# Revit family: WAGNER_Извещатели_TITANUS PRO SENS_net
name_source: partatom
category: Оборудование
revit_build: Autodesk Revit 2017 (Build: 20170118_1100(x64)
units: mm (PartAtom-declared; Revit-internal decimal feet)

## family parameters
Всегда вертикально = Да
Заголовок OmniClass = Alarm Panels
На основе рабочей плоскости = Нет
Номер OmniClass = 23.85.30.21.11.14
Общий = Да
При загрузке вырезать с полостями = Нет
Размер круглого соединителя = Использовать диаметр
Тип детали = Нормальный
Точка расчета площади = Нет

## types (6) — shared parameters
ADSK_URL документации изделия = https://ru.wagnergroup.com
ADSK_URL страницы изделия = https://ru.wagnergroup.com
ADSK_Версия Revit = Revit 2017
ADSK_Версия семейства = Версия 1
ADSK_Дата изменения = 18.07.20
ADSK_Единица измерения = шт.
ADSK_Завод-изготовитель = WAGNER
ADSK_Код изделия = -
ADSK_Материал = WAGNER_Корпус
ADSK_Наименование = Извещатель пожарный дымовой аспирационный
ADSK_Наименование краткое = Извещатель пожарный
ADSK_Напряжение = 24 В
ADSK_Размер_Высота = 292 мм
ADSK_Размер_Длина = 200 мм
ADSK_Размер_Ширина = 113 мм
COBie Category = Fire alarm panels
Masterformat Code = 28 46 23
Masterformat Title = Fire Alarm Notification Appliances
OmniClass Code = 23.85.30.21.11.14
OmniClass Title = Alarm Panels
UNSPSC Code = 46191505
UNSPSC Title = Fire alarm systems
URL = www.wagner-russia.com
Uniclass Code = Pr_75_75_30_29
Uniclass Title = Fire alarm panels
WAGNER_Ip = Ip20 или Ip52
WAGNER_Классы проектирования  = А, B, C
WAGNER_Количество каналов обнаружения = 2
WAGNER_Количество сигналов (реле) неисправности = от 1 до 2
WAGNER_Питание = 24В
WAGNER_Расчет системы = Программа PipeCalc
WAGNER_Страна производства = Германия
bimon.ru = bimon.ru
Изготовитель = WAGNER
Описание = Извещатель пожарный дымовой аспирационный

## per-type parameters (varying)
| type | ADSK_Марка | WAGNER_Variation | WAGNER_Артикул | WAGNER_Количество сигналов (реле) тревоги | WAGNER_Модуль управления вентилятором | WAGNER_Название | WAGNER_Плата_сетевая_TITANUS_NU-5-D | WAGNER_Температурный режим. | WAGNER_Тип | WAGNER_Тип детекторных модулей | WAGNER_Уровень шума  | WAGNER_Чувствительность |
| Typ TP-4 AD-05-0462 | Typ TP-4 | 1 | AD-05-0462 | от 1 до 4 | Да | Извещатель пожарный дымовой аспирационный TITANUS PRO·SENS/net | Да | от -20℃ до +60℃ | Typ TP-4 | DM-TT-50L, DM-TT-10L, DM-TT-01L | 45 дБ | от 0,01 %/м до 0,5 %/м |
| Typ TP-5 AD-05-0665 | Typ TP-5 | 2 | AD-05-0665 | от 1 до 6 | Да | Извещатель пожарный дымовой аспирационный TITANUS PRO·SENS/net | Да | от -20℃ до +60℃ | Typ TP-5 | DM-TT-50L, DM-TT-10L, DM-TT-01L | 45 дБ | от 0,0049 %/м до 0,5 %/м |
| Typ TP-4-SL AD-05-0459 | Typ TP-4-SL | 3 | AD-05-0459 | от 1 до 4 | Да | Извещатель пожарный дымовой аспирационный TITANUS PRO·SENS/net бесшумная версия | Да | от -20℃ до +60℃ | Typ TP-4-SL | DM-TT-50L, DM-TT-10L, DM-TT-01L | от 23 дБ до 30 дБ | от 0,01 %/м до 0,5 %/м |
| Typ TP-5-SL AD-05-0667 | Typ TP-5-SL | 4 | AD-05-0667 | от 1 до 6 | Да | Извещатель пожарный дымовой аспирационный TITANUS PRO·SENS/net бесшумная версия | Да | от -20℃ до +60℃ | Typ TP-5-SL | DM-TT-50L, DM-TT-10L, DM-TT-01L | от 23 дБ до 30 дБ | от 0,0049 %/м до 0,5 %/м |
| Typ TP-4-F AD-05-0463 | Typ TP-4-F | 5 | AD-05-0463 | от 1 до 4 | Да | Извещатель пожарный дымовой аспирационный TITANUS PRO·SENS/net низкотемпературная версия | Да | от -40℃ до +60℃ | Typ TP-4-F | DM-TT-50L-F, DM-TT-10L-F, DM-TT-01L-F | 45 дБ | от 0,01 %/м до 0,5 %/м |
| Typ TP-5-F AD-05-0669 | Typ TP-5-F | 6 | AD-05-0669 | от 1 до 6 | Нет | Извещатель пожарный дымовой аспирационный TITANUS PRO·SENS/net низкотемпературная версия | Нет | от -40℃ до +60℃ | Typ TP-5-F | DM-TT-50L-F, DM-TT-10L-F, DM-TT-01L-F | 45 дБ | от 0,0049 %/м до 0,5 %/м |

## geometry (parser evidence)
native form markers: Blend x2
no freeform markers — native parametric forms only
